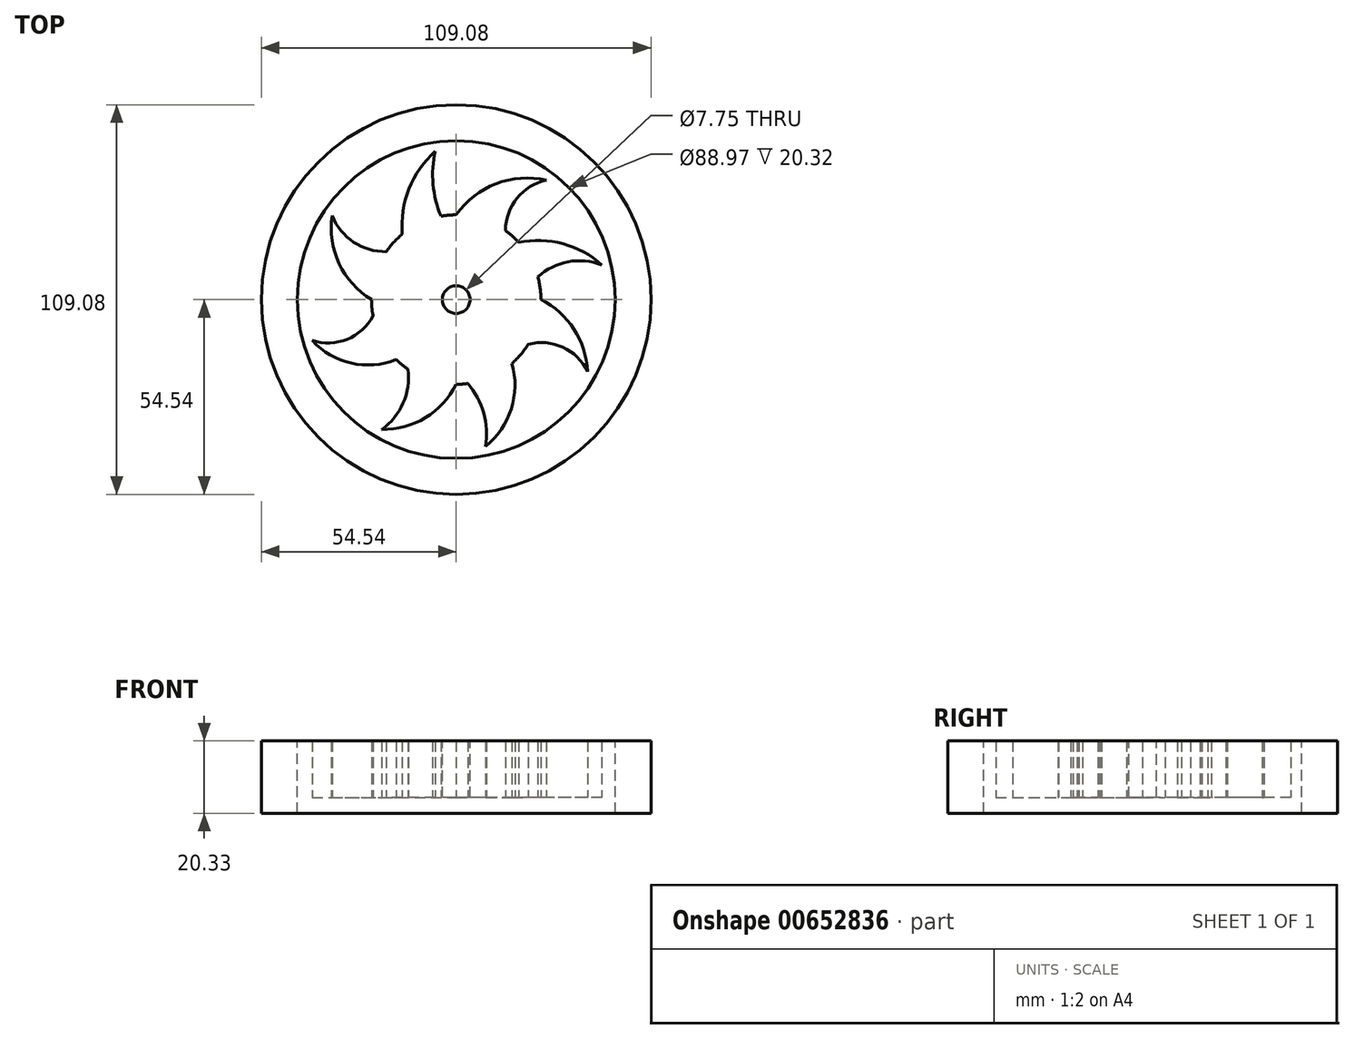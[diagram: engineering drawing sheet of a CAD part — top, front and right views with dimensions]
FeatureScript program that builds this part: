
annotation { "Feature Type Name" : "Feature", "Feature Type Description" : "" }
export const myFeature = defineFeature(function(context is Context, id is Id, definition is map)
    precondition{}
    {
        {
            var Q0;
            Q0=qCreatedBy(makeId("Top.planeOp"),FACE);
            var sketch = newSketch(context, id + "F0", { "sketchPlane" : qUnion([Q0])});
            skCircle(sketch, "E0", {"center": v(0, 0) * mm, "radius": 23.72 * mm});
            skArc(sketch, "E1", {"start": v(25.27, 33.45) * mm, "mid": v(11.16, 32.43) * mm, "end": v(0, 23.72) * mm});
            skArc(sketch, "E2", {"start": v(25.27, 33.45) * mm, "mid": v(17.03, 28.4) * mm, "end": v(13.8, 19.3) * mm});
            skArc(sketch, "E3", {"start": v(36.77, -20.15) * mm, "mid": v(33, -8.3) * mm, "end": v(23.72, 0) * mm});
            skArc(sketch, "E4", {"start": v(36.77, -20.15) * mm, "mid": v(29.84, -13.34) * mm, "end": v(20.15, -12.52) * mm});
            skArc(sketch, "E5", {"start": v(-20.85, -36.37) * mm, "mid": v(-8.6, -33.05) * mm, "end": v(0, -23.72) * mm});
            skArc(sketch, "E6", {"start": v(-20.85, -36.37) * mm, "mid": v(-14.86, -28.96) * mm, "end": v(-13.46, -19.54) * mm});
            skArc(sketch, "E7", {"start": v(-34.73, 23.49) * mm, "mid": v(-32.76, 10.09) * mm, "end": v(-23.72, 0) * mm});
            skArc(sketch, "E8", {"start": v(-34.73, 23.49) * mm, "mid": v(-28.72, 16.08) * mm, "end": v(-19.56, 13.42) * mm});
            skArc(sketch, "E9", {"start": v(-5.84, 41.52) * mm, "mid": v(-13.21, 31) * mm, "end": v(-15.1, 18.3) * mm});
            skArc(sketch, "E10", {"start": v(-5.84, 41.52) * mm, "mid": v(-6.48, 32.3) * mm, "end": v(-4.26, 23.34) * mm});
            skArc(sketch, "E11", {"start": v(40.78, 9.72) * mm, "mid": v(29.88, 15.62) * mm, "end": v(17.49, 16.03) * mm});
            skArc(sketch, "E12", {"start": v(40.78, 9.72) * mm, "mid": v(31.34, 10.58) * mm, "end": v(22.86, 6.33) * mm});
            skArc(sketch, "E13", {"start": v(8.2, -41.12) * mm, "mid": v(15.4, -30.61) * mm, "end": v(15.6, -17.87) * mm});
            skArc(sketch, "E14", {"start": v(8.2, -41.12) * mm, "mid": v(7.69, -31.76) * mm, "end": v(3.24, -23.5) * mm});
            skArc(sketch, "E15", {"start": v(-40.33, -11.45) * mm, "mid": v(-29.4, -17.8) * mm, "end": v(-16.79, -16.76) * mm});
            skArc(sketch, "E16", {"start": v(-40.33, -11.45) * mm, "mid": v(-30.54, -11.11) * mm, "end": v(-23.29, -4.53) * mm});
            skSolve(sketch);
        }
        {
            var Q0;
            {var subQ0=sQuery(id+"F0.wireOp",EDGE,"E0");var subQ8=makeQuery(id+"F0.imprint","INTERSECT",VERTEX,{"derivedFrom":[subQ0,sQuery(id+"F0.wireOp",EDGE,"E3")]});Q0=makeQuery(id+"F0.imprint","IMPRINT",FACE,{"disambiguationData":[TD([[makeQuery(id+"F0.imprint","IMPRINT",EDGE,{"disambiguationData":[TD([[subQ8,-1.0]])],"derivedFrom":subQ0}),1.0]])]});}
            extrude(context, id + "F1", {"entities" : qUnion([Q0]), "depth" : 6.35 * mm, "offsetDistance" : 25.4 * mm});
        }
        {
            var Q0;
            {var subQ0=sQuery(id+"F0.wireOp",EDGE,"E7");Q0=makeQuery(id+"F0.imprint","IMPRINT",FACE,{"disambiguationData":[TD([[makeQuery(id+"F0.imprint","IMPRINT",EDGE,{"derivedFrom":subQ0}),1.0]])]});}
            var Q1;
            {var subQ0=sQuery(id+"F0.wireOp",EDGE,"E15");Q1=makeQuery(id+"F0.imprint","IMPRINT",FACE,{"disambiguationData":[TD([[makeQuery(id+"F0.imprint","IMPRINT",EDGE,{"derivedFrom":subQ0}),1.0]])]});}
            var Q2;
            {var subQ0=sQuery(id+"F0.wireOp",EDGE,"E5");Q2=makeQuery(id+"F0.imprint","IMPRINT",FACE,{"disambiguationData":[TD([[makeQuery(id+"F0.imprint","IMPRINT",EDGE,{"derivedFrom":subQ0}),1.0]])]});}
            var Q3;
            {var subQ0=sQuery(id+"F0.wireOp",EDGE,"E13");Q3=makeQuery(id+"F0.imprint","IMPRINT",FACE,{"disambiguationData":[TD([[makeQuery(id+"F0.imprint","IMPRINT",EDGE,{"derivedFrom":subQ0}),1.0]])]});}
            var Q4;
            {var subQ0=sQuery(id+"F0.wireOp",EDGE,"E3");Q4=makeQuery(id+"F0.imprint","IMPRINT",FACE,{"disambiguationData":[TD([[makeQuery(id+"F0.imprint","IMPRINT",EDGE,{"derivedFrom":subQ0}),1.0]])]});}
            var Q5;
            {var subQ0=sQuery(id+"F0.wireOp",EDGE,"E11");Q5=makeQuery(id+"F0.imprint","IMPRINT",FACE,{"disambiguationData":[TD([[makeQuery(id+"F0.imprint","IMPRINT",EDGE,{"derivedFrom":subQ0}),1.0]])]});}
            var Q6;
            {var subQ0=sQuery(id+"F0.wireOp",EDGE,"E1");Q6=makeQuery(id+"F0.imprint","IMPRINT",FACE,{"disambiguationData":[TD([[makeQuery(id+"F0.imprint","IMPRINT",EDGE,{"derivedFrom":subQ0}),1.0]])]});}
            var Q7;
            {var subQ0=sQuery(id+"F0.wireOp",EDGE,"E9");Q7=makeQuery(id+"F0.imprint","IMPRINT",FACE,{"disambiguationData":[TD([[makeQuery(id+"F0.imprint","IMPRINT",EDGE,{"derivedFrom":subQ0}),1.0]])]});}
            var Q8;
            {var subQ0=sQuery(id+"F0.wireOp",EDGE,"E0");var subQ8=makeQuery(id+"F0.imprint","INTERSECT",VERTEX,{"derivedFrom":[subQ0,sQuery(id+"F0.wireOp",EDGE,"E3")]});Q8=makeQuery(id+"F0.imprint","IMPRINT",FACE,{"disambiguationData":[TD([[makeQuery(id+"F0.imprint","IMPRINT",EDGE,{"disambiguationData":[TD([[subQ8,-1.0]])],"derivedFrom":subQ0}),1.0]])]});}
            extrude(context, id + "F2", {"entities" : qUnion([Q0, Q1, Q2, Q3, Q4, Q5, Q6, Q7, Q8]), "operationType" : NewBodyOperationType.ADD, "depth" : 15.88 * mm, "offsetDistance" : 25.4 * mm});
        }
        {
            var Q0;
            Q0=qCreatedBy(makeId("Top.planeOp"),FACE);
            var sketch = newSketch(context, id + "F3", { "sketchPlane" : qUnion([Q0])});
            skPoint(sketch, "E17", {"position": v(0, 0) * mm});
            skCircle(sketch, "E18", {"center": v(0, 0) * mm, "radius": 0.4 * mm});
            skSolve(sketch);
        }
        {
            var Q0;
            Q0=sQuery(id+"F3.wireOp",VERTEX,"E17");
            var Q1;
            Q1=makeQuery(id+"F1.opExtrude","SWEPT_BODY",BODY,{"disambiguationData":[OSD([sQuery(id+"F0.wireOp",EDGE,"E0")])]});
            hole(context, id + "F4", {"style" : HoleStyle.SIMPLE, "endStyle" : HoleEndStyle.THROUGH, "oppositeDirection" : true, "holeDiameter" : 0.34 * mm, "isTappedThrough" : true, "tappedDepth" : 12.7 * mm, "tapClearance" : 3, "locations" : qUnion([Q0]), "scope" : qUnion([Q1])});
        }
        {
            var Q0;
            Q0=makeQuery(id+"F2.opExtrude","CAP_FACE",FACE,{"disambiguationData":[OSD([sQuery(id+"F0.wireOp",EDGE,"E0"),sQuery(id+"F0.wireOp",EDGE,"E1"),sQuery(id+"F0.wireOp",EDGE,"E2"),sQuery(id+"F0.wireOp",EDGE,"E3"),sQuery(id+"F0.wireOp",EDGE,"E4"),sQuery(id+"F0.wireOp",EDGE,"E5"),sQuery(id+"F0.wireOp",EDGE,"E6"),sQuery(id+"F0.wireOp",EDGE,"E7"),sQuery(id+"F0.wireOp",EDGE,"E8"),sQuery(id+"F0.wireOp",EDGE,"E9"),sQuery(id+"F0.wireOp",EDGE,"E10"),sQuery(id+"F0.wireOp",EDGE,"E11"),sQuery(id+"F0.wireOp",EDGE,"E12"),sQuery(id+"F0.wireOp",EDGE,"E13"),sQuery(id+"F0.wireOp",EDGE,"E14"),sQuery(id+"F0.wireOp",EDGE,"E15"),sQuery(id+"F0.wireOp",EDGE,"E16")])],"isStart":false});
            var sketch = newSketch(context, id + "F5", { "sketchPlane" : qUnion([Q0])});
            skCircle(sketch, "E19", {"center": v(0, 0) * mm, "radius": 44.48 * mm});
            skCircle(sketch, "E20", {"center": v(0, 0) * mm, "radius": 54.54 * mm});
            skSolve(sketch);
        }
        {
            var Q0;
            Q0=makeQuery(id+"F5.imprint","IMPRINT",FACE,{"disambiguationData":[TD([[makeQuery(id+"F5.imprint","IMPRINT",EDGE,{"derivedFrom":sQuery(id+"F5.wireOp",EDGE,"E19")}),-1.0]])]});
            extrude(context, id + "F6", {"entities" : qUnion([Q0]), "oppositeDirection" : true, "depth" : 20.32 * mm, "offsetDistance" : 25.4 * mm});
        }
        {
            var Q0;
            Q0=makeQuery(id+"F2.opExtrude","CAP_FACE",FACE,{"disambiguationData":[OSD([sQuery(id+"F0.wireOp",EDGE,"E0"),sQuery(id+"F0.wireOp",EDGE,"E1"),sQuery(id+"F0.wireOp",EDGE,"E2"),sQuery(id+"F0.wireOp",EDGE,"E3"),sQuery(id+"F0.wireOp",EDGE,"E4"),sQuery(id+"F0.wireOp",EDGE,"E5"),sQuery(id+"F0.wireOp",EDGE,"E6"),sQuery(id+"F0.wireOp",EDGE,"E7"),sQuery(id+"F0.wireOp",EDGE,"E8"),sQuery(id+"F0.wireOp",EDGE,"E9"),sQuery(id+"F0.wireOp",EDGE,"E10"),sQuery(id+"F0.wireOp",EDGE,"E11"),sQuery(id+"F0.wireOp",EDGE,"E12"),sQuery(id+"F0.wireOp",EDGE,"E13"),sQuery(id+"F0.wireOp",EDGE,"E14"),sQuery(id+"F0.wireOp",EDGE,"E15"),sQuery(id+"F0.wireOp",EDGE,"E16")])],"isStart":false});
            var sketch = newSketch(context, id + "F7", { "sketchPlane" : qUnion([Q0])});
            skCircle(sketch, "E21", {"center": v(0, 0) * mm, "radius": 3.87 * mm});
            skSolve(sketch);
        }
        {
            var Q0;
            Q0 = qSketchRegion(id + "F7", true);
            extrude(context, id + "F8", {"entities" : qUnion([Q0]), "operationType" : NewBodyOperationType.REMOVE, "oppositeDirection" : true, "depth" : 25.4 * mm, "offsetDistance" : 25.4 * mm});
        }
    });
